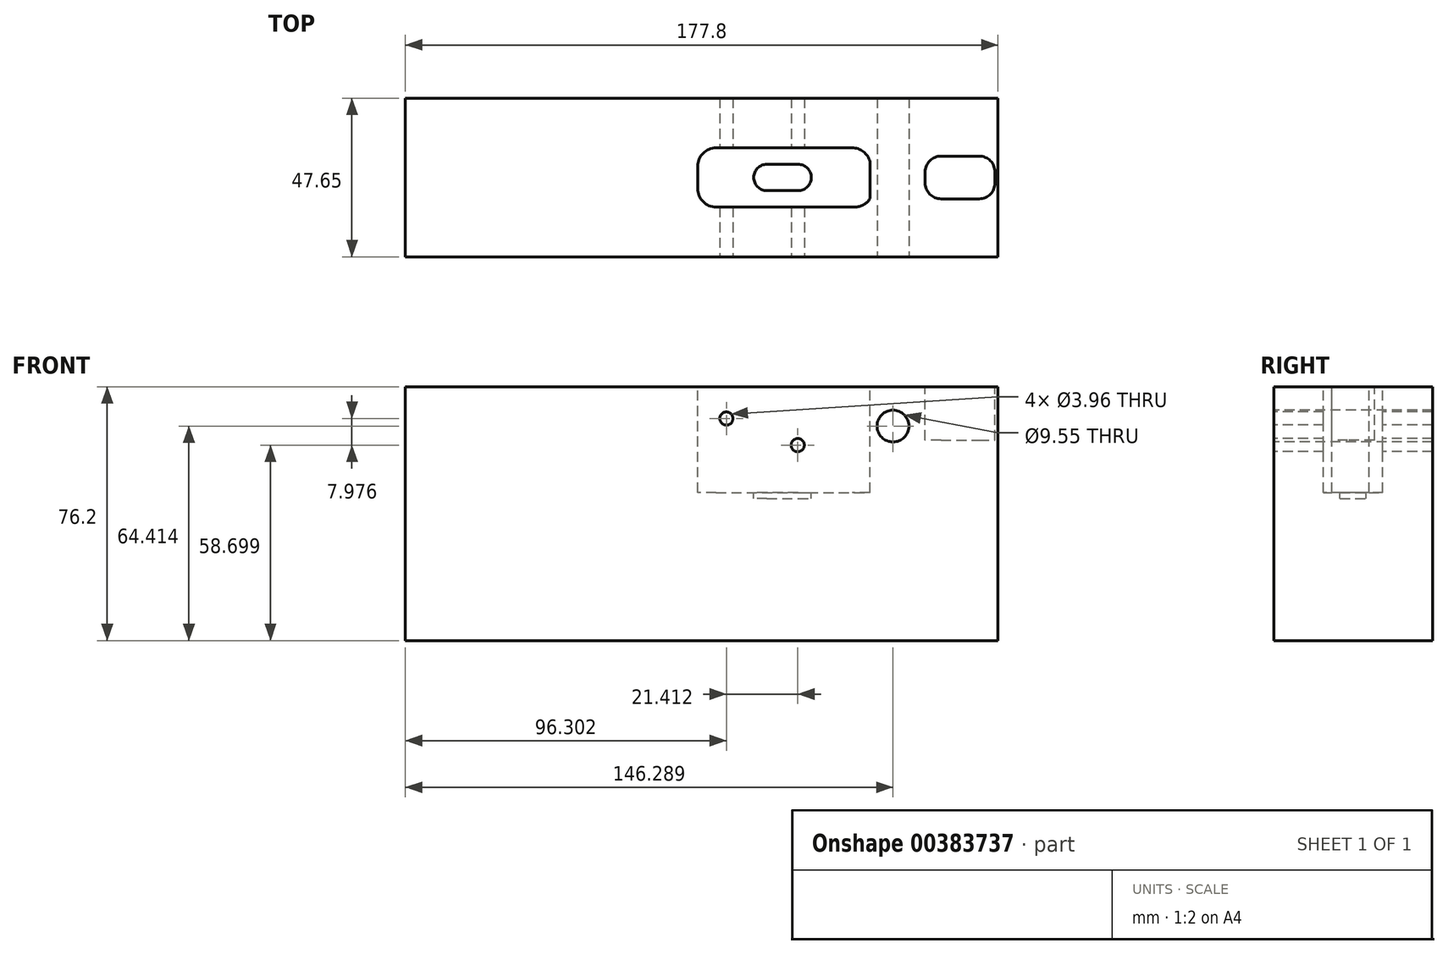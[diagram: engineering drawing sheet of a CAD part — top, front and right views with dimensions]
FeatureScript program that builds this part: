
annotation { "Feature Type Name" : "Feature", "Feature Type Description" : "" }
export const myFeature = defineFeature(function(context is Context, id is Id, definition is map)
    precondition{}
    {
        {
            var Q0;
            Q0=qCreatedBy(makeId("Top.planeOp"),FACE);
            var sketch = newSketch(context, id + "F0", { "sketchPlane" : qUnion([Q0])});
            skLineSegment(sketch, "E0.bottom", {"start": v(-4.76, 47.65) * mm, "end": v(173.04, 47.65) * mm});
            skLineSegment(sketch, "E0.top", {"start": v(-4.76, 0) * mm, "end": v(173.04, 0) * mm});
            skLineSegment(sketch, "E0.left", {"start": v(-4.76, 47.65) * mm, "end": v(-4.76, 0) * mm});
            skLineSegment(sketch, "E0.right", {"start": v(173.04, 47.65) * mm, "end": v(173.04, 0) * mm});
            skLineSegment(sketch, "E1", {"start": v(173, 23.83) * mm, "end": v(-20.73, 23.83) * mm, "construction": true});
            skPoint(sketch, "E1.startSnap0", {"position": v(173.04, 23.83) * mm});
            skPoint(sketch, "E1.endSnap0", {"position": v(-4.76, 23.83) * mm});
            skSolve(sketch);
        }
        {
            var Q0;
            Q0=makeQuery(id+"F0.imprint","IMPRINT",FACE,{"disambiguationData":[TD([[makeQuery(id+"F0.imprint","IMPRINT",EDGE,{"derivedFrom":sQuery(id+"F0.wireOp",EDGE,"E0.bottom")}),-1.0]])]});
            extrude(context, id + "F1", {"entities" : qUnion([Q0]), "oppositeDirection" : true, "depth" : 76.2 * mm});
        }
        {
            var Q0;
            Q0=qCreatedBy(makeId("Front.planeOp"),FACE);
            var sketch = newSketch(context, id + "F2", { "sketchPlane" : qUnion([Q0])});
            skCircle(sketch, "E2", {"center": v(0, 0) * mm, "radius": 3.18 * mm, "construction": true});
            skCircle(sketch, "E3", {"center": v(141.53, -11.79) * mm, "radius": 4.78 * mm});
            skCircle(sketch, "E4", {"center": v(112.95, -17.5) * mm, "radius": 1.98 * mm});
            skCircle(sketch, "E5", {"center": v(91.54, -9.52) * mm, "radius": 1.98 * mm});
            skSolve(sketch);
        }
        {
            var Q0;
            Q0=qSketchRegion(id+"F2",true);
            extrude(context, id + "F3", {"entities" : qUnion([Q0]), "operationType" : NewBodyOperationType.REMOVE, "endBound" : BoundingType.THROUGH_ALL, "oppositeDirection" : true, "depth" : 25.4 * mm});
        }
        {
            var Q0;
            Q0=makeQuery(id+"F0.imprint","IMPRINT",FACE,{"disambiguationData":[TD([[makeQuery(id+"F0.imprint","IMPRINT",EDGE,{"derivedFrom":sQuery(id+"F0.wireOp",EDGE,"E0.bottom")}),-1.0]])]});
            var sketch = newSketch(context, id + "F4", { "sketchPlane" : qUnion([Q0])});
            skLineSegment(sketch, "E6.right", {"start": v(172.14, 25.46) * mm, "end": v(172.14, 22.19) * mm});
            skPoint(sketch, "E7.visualSharp", {"position": v(172.14, 30.23) * mm});
            skPoint(sketch, "E8.visualSharp", {"position": v(172.14, 17.42) * mm});
            skPoint(sketch, "E9.visualSharp", {"position": v(142.53, 46.05) * mm});
            skLineSegment(sketch, "E10", {"start": v(155.94, 30.23) * mm, "end": v(167.37, 30.23) * mm});
            skLineSegment(sketch, "E11", {"start": v(0, 63.67) * mm, "end": v(0, 0) * mm, "construction": true});
            skLineSegment(sketch, "E12", {"start": v(157.52, 17.42) * mm, "end": v(167.37, 17.42) * mm});
            skLineSegment(sketch, "E13", {"start": v(151.18, 25.46) * mm, "end": v(151.18, 22.19) * mm});
            skLineSegment(sketch, "E14", {"start": v(155.94, 17.42) * mm, "end": v(157.52, 17.42) * mm});
            skPoint(sketch, "E15.visualSharp", {"position": v(151.18, 30.23) * mm});
            skArc(sketch, "E15.filletArc", {"start": v(155.94, 30.23) * mm, "mid": v(152.58, 28.83) * mm, "end": v(151.18, 25.46) * mm});
            skPoint(sketch, "E16.visualSharp", {"position": v(151.18, 17.42) * mm});
            skArc(sketch, "E16.filletArc", {"start": v(151.18, 22.19) * mm, "mid": v(152.58, 18.82) * mm, "end": v(155.94, 17.42) * mm});
            skArc(sketch, "E17.filletArc", {"start": v(172.14, 25.46) * mm, "mid": v(170.74, 28.83) * mm, "end": v(167.37, 30.23) * mm});
            skArc(sketch, "E18.filletArc", {"start": v(167.37, 17.42) * mm, "mid": v(170.74, 18.82) * mm, "end": v(172.14, 22.19) * mm});
            skSolve(sketch);
        }
        {
            var Q0;
            Q0=qSketchRegion(id+"F4",true);
            extrude(context, id + "F5", {"entities" : qUnion([Q0]), "operationType" : NewBodyOperationType.REMOVE, "oppositeDirection" : true, "depth" : 16 * mm});
        }
        {
            var Q0;
            Q0=makeQuery(id+"F0.imprint","IMPRINT",FACE,{"disambiguationData":[TD([[makeQuery(id+"F0.imprint","IMPRINT",EDGE,{"derivedFrom":sQuery(id+"F0.wireOp",EDGE,"E0.bottom")}),-1.0]])]});
            var sketch = newSketch(context, id + "F6", { "sketchPlane" : qUnion([Q0])});
            skLineSegment(sketch, "E19.bottom", {"start": v(103.7, 27.78) * mm, "end": v(113.06, 27.78) * mm});
            skLineSegment(sketch, "E19.top", {"start": v(103.7, 19.86) * mm, "end": v(113.06, 19.86) * mm});
            skLineSegment(sketch, "E19.left", {"start": v(99.75, 23.82) * mm, "end": v(99.75, 23.82) * mm});
            skLineSegment(sketch, "E19.right", {"start": v(117.02, 23.82) * mm, "end": v(117.02, 23.82) * mm});
            skPoint(sketch, "E20.visualSharp", {"position": v(99.75, 27.78) * mm});
            skArc(sketch, "E20.filletArc", {"start": v(103.7, 27.78) * mm, "mid": v(100.9, 26.62) * mm, "end": v(99.75, 23.82) * mm});
            skPoint(sketch, "E21.visualSharp", {"position": v(117.02, 27.78) * mm});
            skArc(sketch, "E21.filletArc", {"start": v(117.02, 23.82) * mm, "mid": v(115.86, 26.62) * mm, "end": v(113.06, 27.78) * mm});
            skPoint(sketch, "E22.visualSharp", {"position": v(117.02, 19.86) * mm});
            skArc(sketch, "E22.filletArc", {"start": v(113.06, 19.86) * mm, "mid": v(115.86, 21.02) * mm, "end": v(117.02, 23.82) * mm});
            skPoint(sketch, "E23.visualSharp", {"position": v(99.75, 19.86) * mm});
            skArc(sketch, "E23.filletArc", {"start": v(99.75, 23.82) * mm, "mid": v(100.9, 21.02) * mm, "end": v(103.7, 19.86) * mm});
            skSolve(sketch);
        }
        {
            var Q0;
            Q0=qSketchRegion(id+"F6",true);
            extrude(context, id + "F7", {"entities" : qUnion([Q0]), "operationType" : NewBodyOperationType.REMOVE, "oppositeDirection" : true, "depth" : 33.53 * mm});
        }
        {
            var Q0;
            Q0=qCreatedBy(makeId("Top.planeOp"),FACE);
            var sketch = newSketch(context, id + "F8", { "sketchPlane" : qUnion([Q0])});
            skLineSegment(sketch, "E24.right", {"start": v(148, 23.06) * mm, "end": v(148, 23.01) * mm});
            skPoint(sketch, "E25.visualSharp", {"position": v(148, 28.6) * mm});
            skPoint(sketch, "E26.visualSharp", {"position": v(148, 17.48) * mm});
            skPoint(sketch, "E27.visualSharp", {"position": v(131.4, 28.6) * mm});
            skPoint(sketch, "E28.visualSharp", {"position": v(131.4, 17.48) * mm});
            skLineSegment(sketch, "E29.bottom", {"start": v(88.47, 32.72) * mm, "end": v(129.26, 32.72) * mm});
            skLineSegment(sketch, "E29.top", {"start": v(88.47, 14.94) * mm, "end": v(130, 14.94) * mm});
            skLineSegment(sketch, "E29.left", {"start": v(82.93, 27.18) * mm, "end": v(82.93, 20.47) * mm});
            skArc(sketch, "E30.filletArc", {"start": v(134.61, 28.6) * mm, "mid": v(132.63, 31.57) * mm, "end": v(129.26, 32.72) * mm});
            skArc(sketch, "E31.filletArc", {"start": v(130, 14.94) * mm, "mid": v(132.65, 15.61) * mm, "end": v(134.66, 17.48) * mm});
            skArc(sketch, "E32.filletArc", {"start": v(88.47, 32.72) * mm, "mid": v(84.55, 31.1) * mm, "end": v(82.93, 27.18) * mm});
            skArc(sketch, "E33.filletArc", {"start": v(82.93, 20.47) * mm, "mid": v(84.55, 16.56) * mm, "end": v(88.47, 14.94) * mm});
            skLineSegment(sketch, "E34", {"start": v(53.04, 23.83) * mm, "end": v(165.2, 23.83) * mm, "construction": true});
            skLineSegment(sketch, "E35", {"start": v(134.61, 28.6) * mm, "end": v(134.66, 17.48) * mm});
            skSolve(sketch);
        }
        {
            var Q0;
            Q0=qSketchRegion(id+"F8",true);
            extrude(context, id + "F9", {"entities" : qUnion([Q0]), "operationType" : NewBodyOperationType.REMOVE, "oppositeDirection" : true, "depth" : 31.72 * mm});
        }
    });
